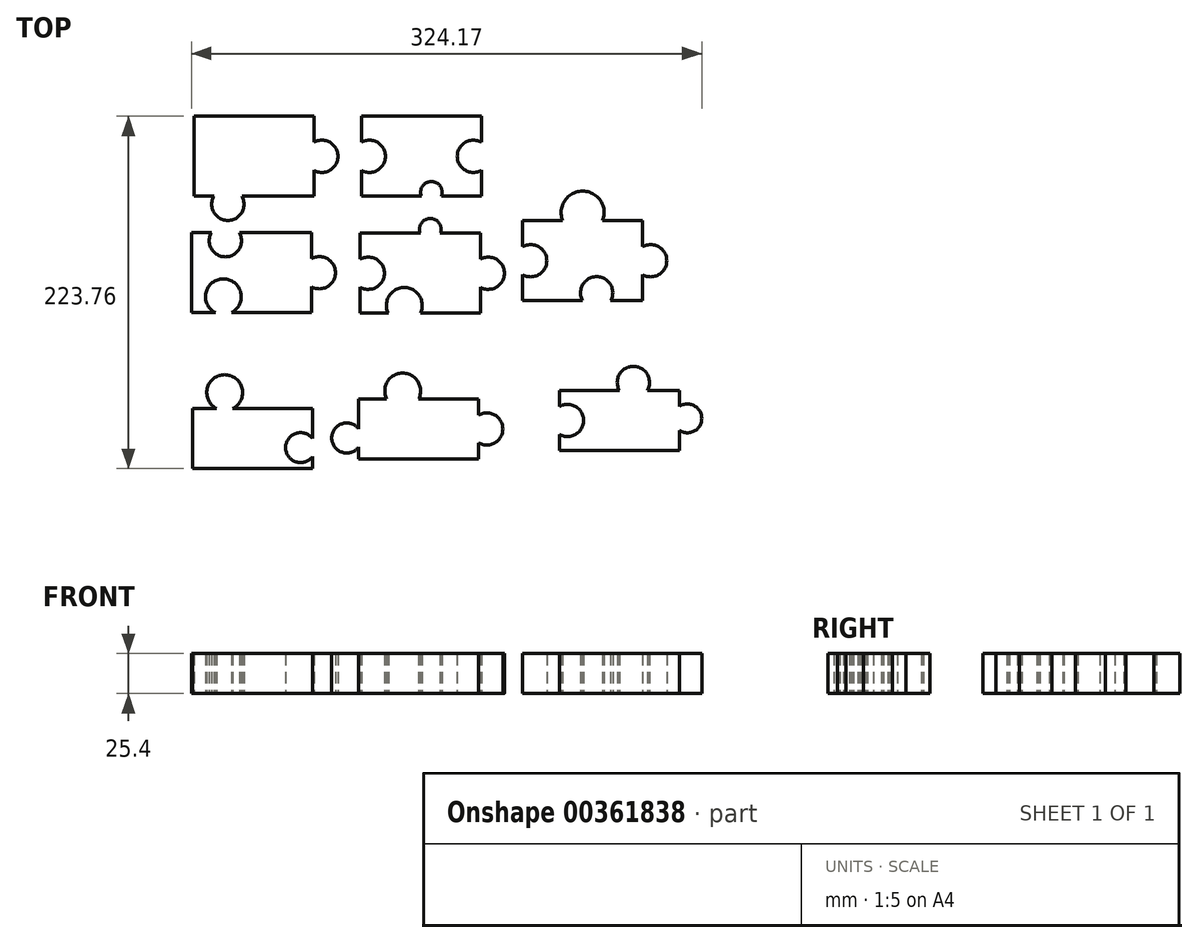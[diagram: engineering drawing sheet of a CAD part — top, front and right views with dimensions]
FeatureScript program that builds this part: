
annotation { "Feature Type Name" : "Feature", "Feature Type Description" : "" }
export const myFeature = defineFeature(function(context is Context, id is Id, definition is map)
    precondition{}
    {
        {
            var Q0;
            Q0=qCreatedBy(makeId("Top.planeOp"),FACE);
            var sketch = newSketch(context, id + "F0", { "sketchPlane" : qUnion([Q0])});
            skLineSegment(sketch, "E0.bottom", {"start": v(0, 0) * mm, "end": v(76.2, 0) * mm});
            skLineSegment(sketch, "E0.top", {"start": v(0, 50.8) * mm, "end": v(76.2, 50.8) * mm});
            skLineSegment(sketch, "E0.left", {"start": v(0, 0) * mm, "end": v(0, 50.8) * mm});
            skLineSegment(sketch, "E0.right", {"start": v(76.2, 0) * mm, "end": v(76.2, 50.8) * mm});
            skArc(sketch, "E1", {"start": v(0, 16.51) * mm, "mid": v(15.32, 25.4) * mm, "end": v(0, 34.3) * mm});
            skArc(sketch, "E2", {"start": v(50.8, 0) * mm, "mid": v(44.45, 9.38) * mm, "end": v(38.1, 0) * mm});
            skArc(sketch, "E3", {"start": v(76.2, 34.3) * mm, "mid": v(60.88, 25.4) * mm, "end": v(76.2, 16.51) * mm});
            skSolve(sketch);
        }
        {
            var Q0;
            Q0 = qSketchRegion(id + "F2", true);
            var Q1;
            {var subQ4=sQuery(id+"F0.wireOp",EDGE,"E0.top");Q1=makeQuery(id+"F0.imprint","IMPRINT",FACE,{"disambiguationData":[TD([[makeQuery(id+"F0.imprint","IMPRINT",EDGE,{"derivedFrom":subQ4}),-1.0]])]});}
            var Q2;
            Q2 = qConstructionFilter(qBodyType(qCreatedBy(id + "F0" ,EDGE), BodyType.WIRE), ConstructionObject.NO);
            extrude(context, id + "F1", {"entities" : qUnion([Q0, Q1]), "surfaceEntities" : qUnion([Q2]), "depth" : 25.4 * mm});
        }
        {
            var Q0;
            Q0=qCreatedBy(makeId("Top.planeOp"),FACE);
            var sketch = newSketch(context, id + "F2", { "sketchPlane" : qUnion([Q0])});
            skLineSegment(sketch, "E4.bottom", {"start": v(-30.2, 50.8) * mm, "end": v(-106.4, 50.8) * mm});
            skLineSegment(sketch, "E4.top", {"start": v(-30.2, 0) * mm, "end": v(-106.4, 0) * mm});
            skLineSegment(sketch, "E4.left", {"start": v(-30.2, 50.8) * mm, "end": v(-30.2, 0) * mm});
            skLineSegment(sketch, "E4.right", {"start": v(-106.4, 50.8) * mm, "end": v(-106.4, 0) * mm});
            skArc(sketch, "E5", {"start": v(-30.2, 16.51) * mm, "mid": v(-14.88, 25.4) * mm, "end": v(-30.2, 34.3) * mm});
            skArc(sketch, "E6", {"start": v(-93.7, 0) * mm, "mid": v(-84.8, -15.32) * mm, "end": v(-75.92, 0) * mm});
            skSolve(sketch);
        }
        {
            var Q0;
            Q0 = qSketchRegion(id + "F2", true);
            extrude(context, id + "F3", {"entities" : qUnion([Q0]), "depth" : 25.4 * mm});
        }
        {
            var Q0;
            Q0=qCreatedBy(makeId("Top.planeOp"),FACE);
            var sketch = newSketch(context, id + "F4", { "sketchPlane" : qUnion([Q0])});
            skLineSegment(sketch, "E7.bottom", {"start": v(-31.78, -23.13) * mm, "end": v(-107.98, -23.13) * mm});
            skLineSegment(sketch, "E7.top", {"start": v(-31.78, -73.93) * mm, "end": v(-107.98, -73.93) * mm});
            skLineSegment(sketch, "E7.left", {"start": v(-31.78, -23.13) * mm, "end": v(-31.78, -73.93) * mm});
            skLineSegment(sketch, "E7.right", {"start": v(-107.98, -23.13) * mm, "end": v(-107.98, -73.93) * mm});
            skArc(sketch, "E8", {"start": v(-95.28, -23.13) * mm, "mid": v(-86.4, -38.45) * mm, "end": v(-77.5, -23.13) * mm});
            skArc(sketch, "E9", {"start": v(-31.78, -57.42) * mm, "mid": v(-16.46, -48.53) * mm, "end": v(-31.78, -39.64) * mm});
            skArc(sketch, "E10", {"start": v(-82.58, -73.93) * mm, "mid": v(-87.66, -52.4) * mm, "end": v(-92.74, -73.93) * mm});
            skSolve(sketch);
        }
        {
            var Q0;
            Q0=makeQuery(id+"F4.imprint","IMPRINT",FACE,{"disambiguationData":[TD([[makeQuery(id+"F4.imprint","IMPRINT",EDGE,{"derivedFrom":sQuery(id+"F4.wireOp",EDGE,"E7.top")}),-1.0]])]});
            var Q1;
            {var subQ0=sQuery(id+"F4.wireOp",EDGE,"E9");Q1=makeQuery(id+"F4.imprint","IMPRINT",FACE,{"disambiguationData":[TD([[makeQuery(id+"F4.imprint","IMPRINT",EDGE,{"derivedFrom":subQ0}),1.0]])]});}
            extrude(context, id + "F5", {"entities" : qUnion([Q0, Q1]), "depth" : 25.4 * mm});
        }
        {
            var Q0;
            Q0=qCreatedBy(makeId("Top.planeOp"),FACE);
            var sketch = newSketch(context, id + "F6", { "sketchPlane" : qUnion([Q0])});
            skLineSegment(sketch, "E11.bottom", {"start": v(-0.7, -23.47) * mm, "end": v(75.5, -23.47) * mm});
            skLineSegment(sketch, "E11.top", {"start": v(-0.7, -74.27) * mm, "end": v(75.5, -74.27) * mm});
            skLineSegment(sketch, "E11.left", {"start": v(-0.7, -23.47) * mm, "end": v(-0.7, -74.27) * mm});
            skLineSegment(sketch, "E11.right", {"start": v(75.5, -23.47) * mm, "end": v(75.5, -74.27) * mm});
            skArc(sketch, "E12", {"start": v(-0.7, -57.76) * mm, "mid": v(14.63, -48.87) * mm, "end": v(-0.7, -39.98) * mm});
            skArc(sketch, "E13", {"start": v(50.1, -23.47) * mm, "mid": v(43.76, -14.1) * mm, "end": v(37.4, -23.47) * mm});
            skArc(sketch, "E14", {"start": v(75.5, -57.76) * mm, "mid": v(90.83, -48.87) * mm, "end": v(75.5, -39.98) * mm});
            skArc(sketch, "E15", {"start": v(37.4, -74.27) * mm, "mid": v(27.25, -57.83) * mm, "end": v(17.09, -74.27) * mm});
            skSolve(sketch);
        }
        {
            var Q0;
            {var subQ4=sQuery(id+"F6.wireOp",EDGE,"BERyK6gC-mRjc-QDPR-Mfbr-4erOwyCjJ1wt.top");Q0=makeQuery(id+"F6.imprint","IMPRINT",FACE,{"disambiguationData":[TD([[makeQuery(id+"F6.imprint","IMPRINT",EDGE,{"derivedFrom":subQ4}),1.0]])]});}
            var Q1;
            {var subQ0=sQuery(id+"F6.wireOp",EDGE,"E13");Q1=makeQuery(id+"F6.imprint","IMPRINT",FACE,{"disambiguationData":[TD([[makeQuery(id+"F6.imprint","IMPRINT",EDGE,{"derivedFrom":subQ0}),1.0]])]});}
            var Q2;
            {var subQ0=sQuery(id+"F6.wireOp",EDGE,"E14");Q2=makeQuery(id+"F6.imprint","IMPRINT",FACE,{"disambiguationData":[TD([[makeQuery(id+"F6.imprint","IMPRINT",EDGE,{"derivedFrom":subQ0}),1.0]])]});}
            var Q3;
            {var subQ9=sQuery(id+"F6.wireOp",EDGE,"E12");Q3=makeQuery(id+"F6.imprint","IMPRINT",FACE,{"disambiguationData":[TD([[makeQuery(id+"F6.imprint","IMPRINT",EDGE,{"derivedFrom":subQ9}),-1.0]])]});}
            extrude(context, id + "F7", {"entities" : qUnion([Q0, Q1, Q2, Q3]), "depth" : 25.4 * mm});
        }
        {
            var Q0;
            {var subQ3=sQuery(id+"F0.wireOp",EDGE,"E0.bottom");Q0=makeQuery(id+"F0.imprint","IMPRINT",FACE,{"disambiguationData":[TD([[makeQuery(id+"F0.imprint","IMPRINT",EDGE,{"derivedFrom":subQ3}),1.0]])]});}
            var Q1;
            Q1 = qSketchRegion(id + "F9", true);
            extrude(context, id + "F8", {"entities" : qUnion([Q0, Q1]), "depth" : 25.4 * mm});
        }
        {
            var Q0;
            Q0=qCreatedBy(makeId("Top.planeOp"),FACE);
            var sketch = newSketch(context, id + "F9", { "sketchPlane" : qUnion([Q0])});
            skLineSegment(sketch, "E16.bottom", {"start": v(102.43, -15.5) * mm, "end": v(178.63, -15.5) * mm});
            skLineSegment(sketch, "E16.top", {"start": v(102.43, -66.3) * mm, "end": v(178.63, -66.3) * mm});
            skLineSegment(sketch, "E16.left", {"start": v(102.43, -15.5) * mm, "end": v(102.43, -66.3) * mm});
            skLineSegment(sketch, "E16.right", {"start": v(178.63, -15.5) * mm, "end": v(178.63, -66.3) * mm});
            skArc(sketch, "E17", {"start": v(153.23, -15.5) * mm, "mid": v(140.53, 3.25) * mm, "end": v(127.83, -15.5) * mm});
            skArc(sketch, "E18", {"start": v(102.43, -49.8) * mm, "mid": v(117.75, -40.9) * mm, "end": v(102.43, -32.02) * mm});
            skArc(sketch, "E19", {"start": v(178.63, -49.8) * mm, "mid": v(193.95, -40.9) * mm, "end": v(178.63, -32.02) * mm});
            skArc(sketch, "E20", {"start": v(158.31, -66.3) * mm, "mid": v(149.42, -50.99) * mm, "end": v(140.53, -66.3) * mm});
            skSolve(sketch);
        }
        {
            var Q0;
            {var subQ0=sQuery(id+"F9.wireOp",EDGE,"E17");Q0=makeQuery(id+"F9.imprint","IMPRINT",FACE,{"disambiguationData":[TD([[makeQuery(id+"F9.imprint","IMPRINT",EDGE,{"derivedFrom":subQ0}),1.0]])]});}
            var Q1;
            {var subQ0=sQuery(id+"F9.wireOp",EDGE,"E19");Q1=makeQuery(id+"F9.imprint","IMPRINT",FACE,{"disambiguationData":[TD([[makeQuery(id+"F9.imprint","IMPRINT",EDGE,{"derivedFrom":subQ0}),1.0]])]});}
            var Q2;
            {var subQ9=sQuery(id+"F9.wireOp",EDGE,"E18");Q2=makeQuery(id+"F9.imprint","IMPRINT",FACE,{"disambiguationData":[TD([[makeQuery(id+"F9.imprint","IMPRINT",EDGE,{"derivedFrom":subQ9}),-1.0]])]});}
            extrude(context, id + "F10", {"entities" : qUnion([Q0, Q1, Q2]), "depth" : 25.4 * mm});
        }
        {
            var Q0;
            Q0=qCreatedBy(makeId("Top.planeOp"),FACE);
            var sketch = newSketch(context, id + "F11", { "sketchPlane" : qUnion([Q0])});
            skLineSegment(sketch, "E21.bottom", {"start": v(-107.18, -134.86) * mm, "end": v(-30.98, -134.86) * mm});
            skLineSegment(sketch, "E21.top", {"start": v(-107.18, -172.96) * mm, "end": v(-30.98, -172.96) * mm});
            skLineSegment(sketch, "E21.left", {"start": v(-107.18, -134.86) * mm, "end": v(-107.18, -172.96) * mm});
            skLineSegment(sketch, "E21.right", {"start": v(-30.98, -134.86) * mm, "end": v(-30.98, -172.96) * mm});
            skArc(sketch, "E22", {"start": v(-81.78, -134.86) * mm, "mid": v(-86.86, -113.34) * mm, "end": v(-91.94, -134.86) * mm});
            skArc(sketch, "E23", {"start": v(-30.98, -153.9) * mm, "mid": v(-48.12, -159.62) * mm, "end": v(-30.98, -165.34) * mm});
            skSolve(sketch);
        }
        {
            var Q0;
            {var subQ0=sQuery(id+"F11.wireOp",EDGE,"E22");Q0=makeQuery(id+"F11.imprint","IMPRINT",FACE,{"disambiguationData":[TD([[makeQuery(id+"F11.imprint","IMPRINT",EDGE,{"derivedFrom":subQ0}),1.0]])]});}
            var Q1;
            {var subQ0=sQuery(id+"F11.wireOp",EDGE,"E21.top");Q1=makeQuery(id+"F11.imprint","IMPRINT",FACE,{"disambiguationData":[TD([[makeQuery(id+"F11.imprint","IMPRINT",EDGE,{"derivedFrom":subQ0}),1.0]])]});}
            extrude(context, id + "F12", {"entities" : qUnion([Q0, Q1]), "depth" : 25.4 * mm});
        }
        {
            var Q0;
            Q0=qCreatedBy(makeId("Top.planeOp"),FACE);
            var sketch = newSketch(context, id + "F13", { "sketchPlane" : qUnion([Q0])});
            skLineSegment(sketch, "E24.bottom", {"start": v(-1.7, -128.74) * mm, "end": v(74.5, -128.74) * mm});
            skLineSegment(sketch, "E24.top", {"start": v(-1.7, -166.84) * mm, "end": v(74.5, -166.84) * mm});
            skLineSegment(sketch, "E24.left", {"start": v(-1.7, -128.74) * mm, "end": v(-1.7, -166.84) * mm});
            skLineSegment(sketch, "E24.right", {"start": v(74.5, -128.74) * mm, "end": v(74.5, -166.84) * mm});
            skArc(sketch, "E25", {"start": v(-1.7, -147.8) * mm, "mid": v(-18.85, -153.5) * mm, "end": v(-1.7, -159.22) * mm});
            skArc(sketch, "E26", {"start": v(36.4, -128.74) * mm, "mid": v(26.23, -112.3) * mm, "end": v(16.07, -128.74) * mm});
            skArc(sketch, "E27", {"start": v(74.5, -156.68) * mm, "mid": v(89.81, -147.8) * mm, "end": v(74.5, -138.9) * mm});
            skSolve(sketch);
        }
        {
            var Q0;
            Q0 = qSketchRegion(id + "F13", true);
            extrude(context, id + "F14", {"entities" : qUnion([Q0]), "depth" : 25.4 * mm});
        }
        {
            var Q0;
            Q0=qCreatedBy(makeId("Top.planeOp"),FACE);
            var sketch = newSketch(context, id + "F15", { "sketchPlane" : qUnion([Q0])});
            skLineSegment(sketch, "E28.bottom", {"start": v(125.75, -123.3) * mm, "end": v(201.95, -123.3) * mm});
            skLineSegment(sketch, "E28.top", {"start": v(125.75, -161.4) * mm, "end": v(201.95, -161.4) * mm});
            skLineSegment(sketch, "E28.left", {"start": v(125.75, -123.3) * mm, "end": v(125.75, -161.4) * mm});
            skLineSegment(sketch, "E28.right", {"start": v(201.95, -123.3) * mm, "end": v(201.95, -161.4) * mm});
            skArc(sketch, "E29", {"start": v(125.75, -151.24) * mm, "mid": v(141.07, -142.35) * mm, "end": v(125.75, -133.46) * mm});
            skArc(sketch, "E30", {"start": v(181.63, -123.3) * mm, "mid": v(172.74, -107.99) * mm, "end": v(163.85, -123.3) * mm});
            skArc(sketch, "E31", {"start": v(201.95, -148.7) * mm, "mid": v(216.19, -141.08) * mm, "end": v(201.95, -133.46) * mm});
            skSolve(sketch);
        }
        {
            var Q0;
            {var subQ0=sQuery(id+"F15.wireOp",EDGE,"E30");Q0=makeQuery(id+"F15.imprint","IMPRINT",FACE,{"disambiguationData":[TD([[makeQuery(id+"F15.imprint","IMPRINT",EDGE,{"derivedFrom":subQ0}),1.0]])]});}
            var Q1;
            {var subQ0=sQuery(id+"F15.wireOp",EDGE,"E28.top");Q1=makeQuery(id+"F15.imprint","IMPRINT",FACE,{"disambiguationData":[TD([[makeQuery(id+"F15.imprint","IMPRINT",EDGE,{"derivedFrom":subQ0}),1.0]])]});}
            var Q2;
            {var subQ0=sQuery(id+"F15.wireOp",EDGE,"E31");Q2=makeQuery(id+"F15.imprint","IMPRINT",FACE,{"disambiguationData":[TD([[makeQuery(id+"F15.imprint","IMPRINT",EDGE,{"derivedFrom":subQ0}),1.0]])]});}
            extrude(context, id + "F16", {"entities" : qUnion([Q0, Q1, Q2]), "depth" : 25.4 * mm});
        }
    });
